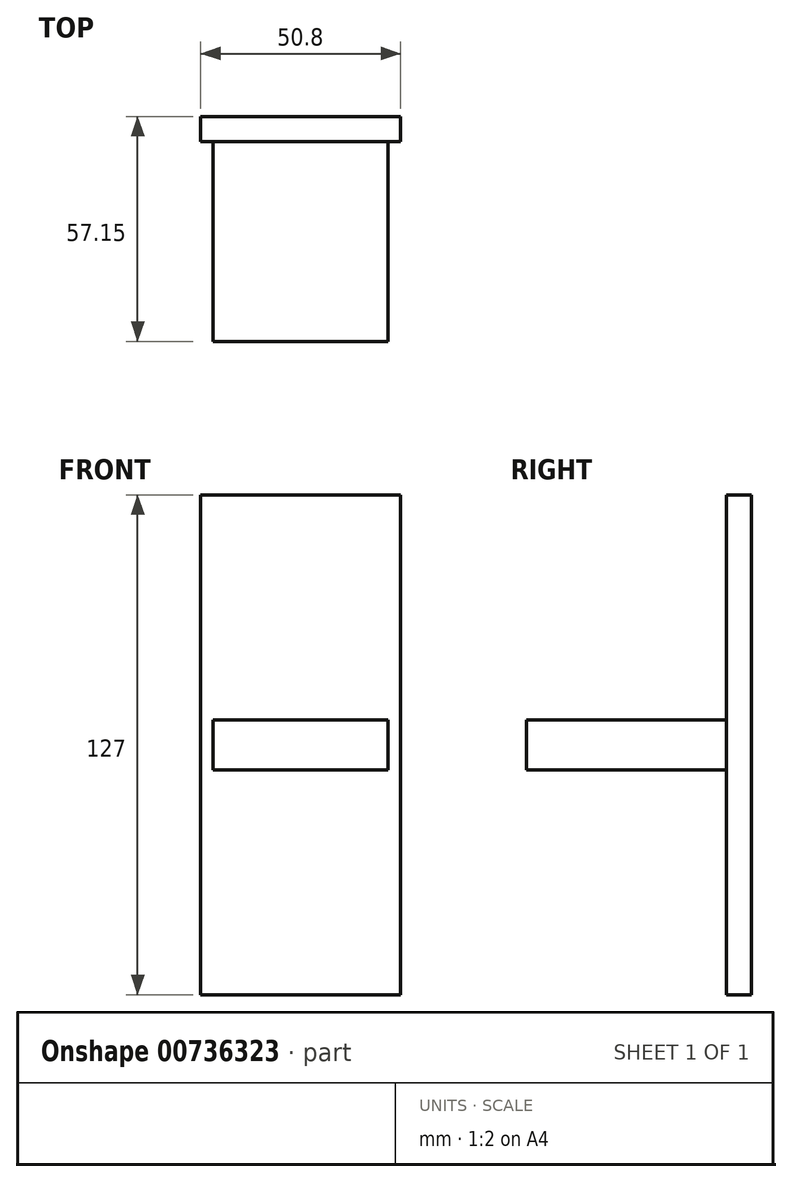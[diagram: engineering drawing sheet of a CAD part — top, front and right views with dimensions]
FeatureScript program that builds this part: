
annotation { "Feature Type Name" : "Feature", "Feature Type Description" : "" }
export const myFeature = defineFeature(function(context is Context, id is Id, definition is map)
    precondition{}
    {
        {
            var Q0;
            Q0=qCreatedBy(makeId("Front.planeOp"),FACE);
            var sketch = newSketch(context, id + "F0", { "sketchPlane" : qUnion([Q0])});
            skLineSegment(sketch, "E0.bottom", {"start": v(25.4, -63.5) * mm, "end": v(-25.4, -63.5) * mm});
            skLineSegment(sketch, "E0.top", {"start": v(25.4, 63.5) * mm, "end": v(-25.4, 63.5) * mm});
            skLineSegment(sketch, "E0.left", {"start": v(25.4, -63.5) * mm, "end": v(25.4, 63.5) * mm});
            skLineSegment(sketch, "E0.right", {"start": v(-25.4, -63.5) * mm, "end": v(-25.4, 63.5) * mm});
            skPoint(sketch, "E0.middle", {"position": v(0, 0) * mm});
            skSolve(sketch);
        }
        {
            var Q0;
            Q0 = qSketchRegion(id + "F0", true);
            extrude(context, id + "F1", {"entities" : qUnion([Q0]), "depth" : 6.35 * mm, "offsetDistance" : 25.4 * mm});
        }
        {
            var Q0;
            Q0=makeQuery(id+"F1.opExtrude","CAP_FACE",FACE,{"disambiguationData":[OSD([sQuery(id+"F0.wireOp",EDGE,"E0.bottom"),sQuery(id+"F0.wireOp",EDGE,"E0.top"),sQuery(id+"F0.wireOp",EDGE,"E0.left"),sQuery(id+"F0.wireOp",EDGE,"E0.right")])],"isStart":false});
            var sketch = newSketch(context, id + "F2", { "sketchPlane" : qUnion([Q0])});
            skSolve(sketch);
        }
        {
            var Q0;
            Q0=makeQuery(id+"F2.imprint","IMPRINT",FACE,{"disambiguationData":[TD([[makeQuery(id+"F2.imprint","IMPRINT",EDGE,{"derivedFrom":makeQuery(id+"F1.opExtrude","CAP_EDGE",EDGE,{"disambiguationData":[OSD([sQuery(id+"F0.wireOp",EDGE,"E0.bottom")])],"isStart":false})}),-1.0]])]});
            var sketch = newSketch(context, id + "F3", { "sketchPlane" : qUnion([Q0])});
            skLineSegment(sketch, "E1.bottom", {"start": v(-22.23, -6.35) * mm, "end": v(22.23, -6.35) * mm});
            skLineSegment(sketch, "E1.top", {"start": v(-22.23, 6.35) * mm, "end": v(22.23, 6.35) * mm});
            skLineSegment(sketch, "E1.left", {"start": v(-22.23, -6.35) * mm, "end": v(-22.23, 6.35) * mm});
            skLineSegment(sketch, "E1.right", {"start": v(22.23, -6.35) * mm, "end": v(22.23, 6.35) * mm});
            skPoint(sketch, "E1.middle", {"position": v(0, 0) * mm});
            skSolve(sketch);
        }
        {
            var Q0;
            Q0 = qSketchRegion(id + "F3", true);
            extrude(context, id + "F4", {"entities" : qUnion([Q0]), "operationType" : NewBodyOperationType.ADD, "depth" : 50.8 * mm, "offsetDistance" : 25.4 * mm});
        }
    });
